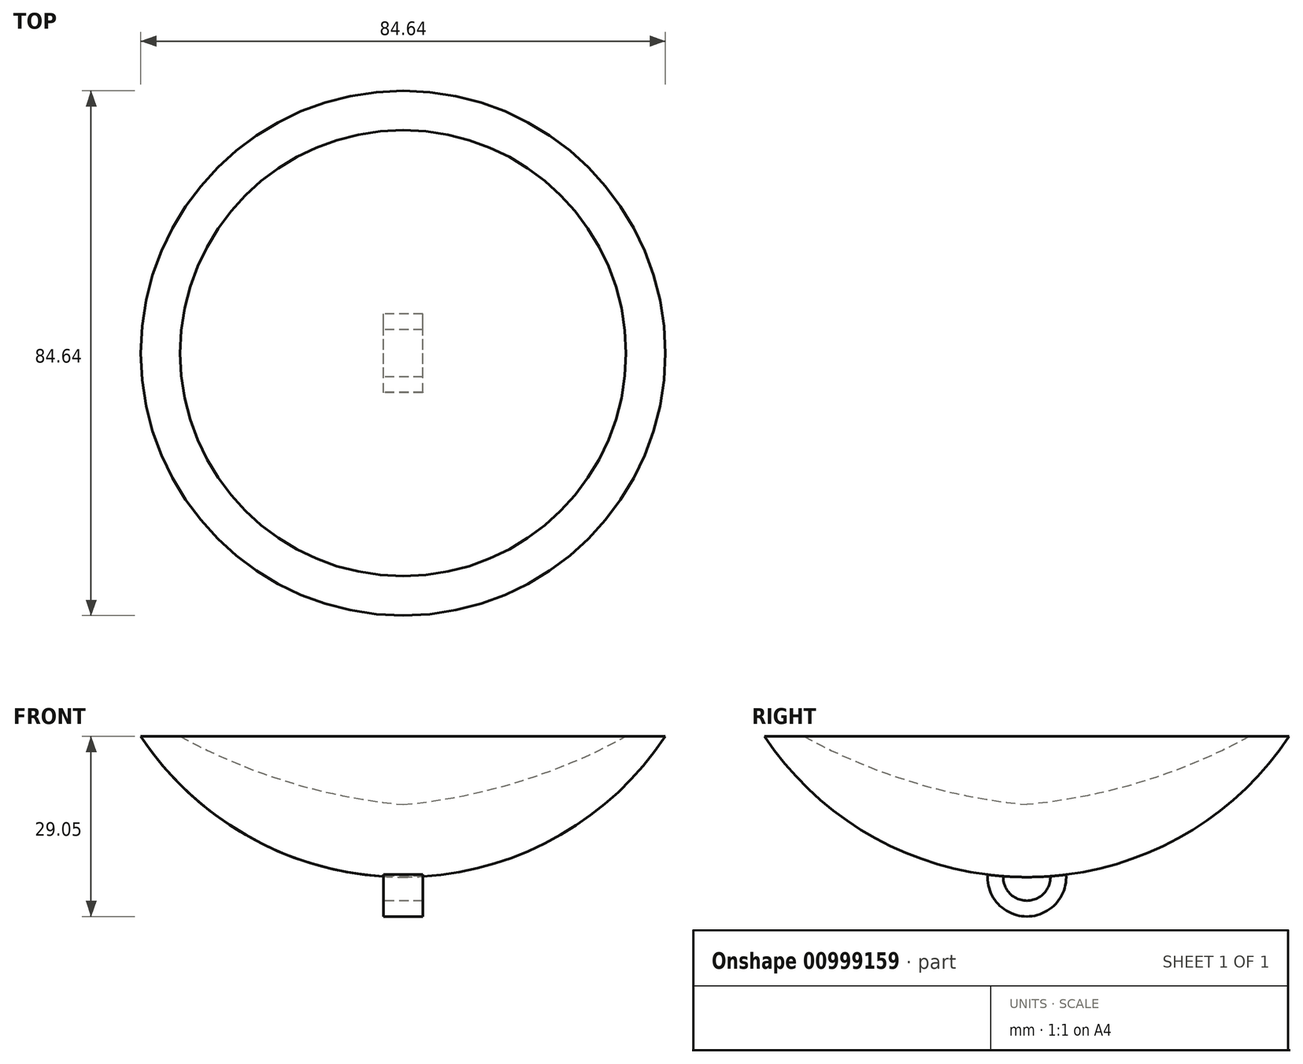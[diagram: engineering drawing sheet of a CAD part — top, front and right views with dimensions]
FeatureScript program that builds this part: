
annotation { "Feature Type Name" : "Feature", "Feature Type Description" : "" }
export const myFeature = defineFeature(function(context is Context, id is Id, definition is map)
    precondition{}
    {
        {
            var Q0;
            Q0=qCreatedBy(makeId("Front.planeOp"),FACE);
            var sketch = newSketch(context, id + "F0", { "sketchPlane" : qUnion([Q0])});
            skArc(sketch, "E0", {"start": v(-42.32, -28.1) * mm, "mid": v(-24.01, -44.77) * mm, "end": v(0, -50.8) * mm});
            skLineSegment(sketch, "E1", {"start": v(0, -44.45) * mm, "end": v(0, -50.8) * mm});
            skPoint(sketch, "E2.start.orphan", {"position": v(50.8, 0) * mm});
            skLineSegment(sketch, "E3", {"start": v(0, -44.45) * mm, "end": v(0, 106.43) * mm});
            skPoint(sketch, "E4.orphan", {"position": v(-50.8, 0) * mm});
            skLineSegment(sketch, "E5", {"start": v(0, -44.45) * mm, "end": v(0, -39.1) * mm});
            skPoint(sketch, "E6.third.point", {"position": v(86.28, 0) * mm});
            skLineSegment(sketch, "E7", {"start": v(-42.32, -28.1) * mm, "end": v(-35.97, -28.1) * mm});
            skArc(sketch, "E8", {"start": v(-35.97, -28.1) * mm, "mid": v(-18.55, -35.44) * mm, "end": v(0, -39.1) * mm});
            skPoint(sketch, "E8.third.point", {"position": v(94.02, 16.66) * mm});
            skSolve(sketch);
        }
        {
            var Q0;
            Q0 = qSketchRegion(id + "F0", true);
            var Q1;
            Q1=sQuery(id+"F0.wireOp",EDGE,"E3");
            revolve(context, id + "F1", {"surfaceOperationType" : NewSurfaceOperationType.NEW, "entities" : qUnion([Q0]), "axis" : qUnion([Q1]), "revolveType" : RevolveType.FULL});
        }
        {
            var Q0;
            Q0=qCreatedBy(makeId("Right.planeOp"),FACE);
            cPlane(context, id + "F2", {"entities" : qUnion([Q0]), "cplaneType" : CPlaneType.OFFSET, "offset" : 3.17 * mm, "oppositeDirection" : true, "width" : 152.4 * mm, "height" : 152.4 * mm});
        }
        {
            var Q0;
            Q0=qCreatedBy(id+"F2.planeOp",FACE);
            var sketch = newSketch(context, id + "F3", { "sketchPlane" : qUnion([Q0])});
            skArc(sketch, "E9", {"start": v(-3.8, -50.66) * mm, "mid": v(0, -54.61) * mm, "end": v(3.8, -50.66) * mm});
            skArc(sketch, "E10", {"start": v(-6.34, -50.4) * mm, "mid": v(0, -57.15) * mm, "end": v(6.34, -50.4) * mm});
            skArc(sketch, "E11", {"start": v(-6.34, -50.4) * mm, "mid": v(-5.07, -50.55) * mm, "end": v(-3.8, -50.66) * mm});
            skArc(sketch, "E12.trimOffspring", {"start": v(3.8, -50.66) * mm, "mid": v(5.07, -50.55) * mm, "end": v(6.34, -50.4) * mm});
            skSolve(sketch);
        }
        {
            var Q0;
            Q0 = qSketchRegion(id + "F3", true);
            extrude(context, id + "F4", {"entities" : qUnion([Q0]), "operationType" : NewBodyOperationType.ADD, "depth" : 6.35 * mm, "offsetDistance" : 25.4 * mm});
        }
    });
